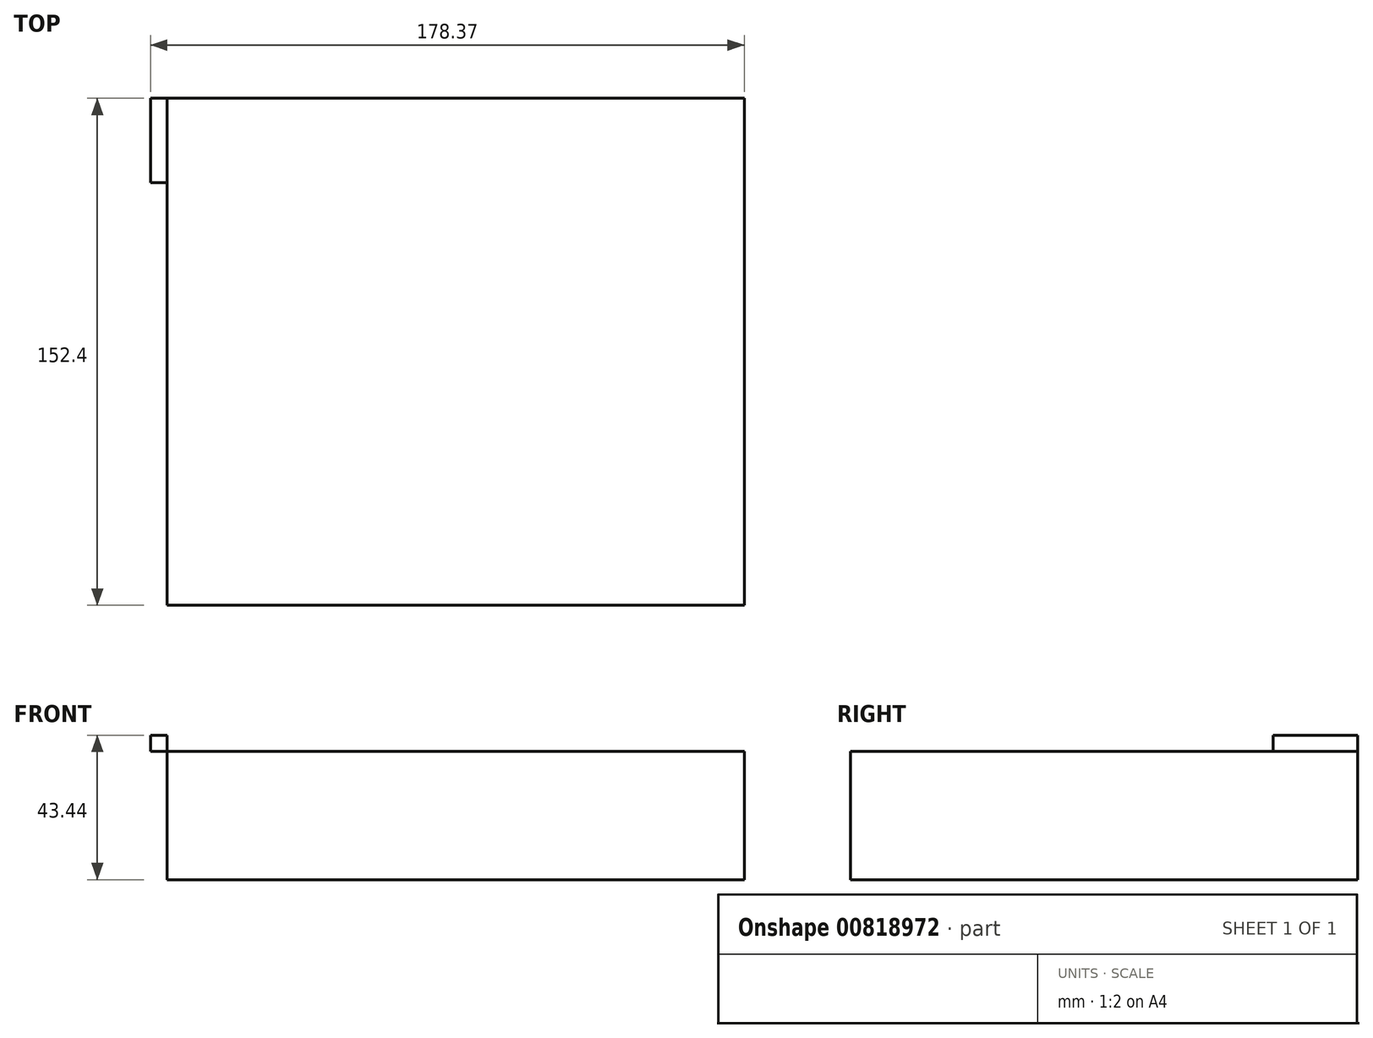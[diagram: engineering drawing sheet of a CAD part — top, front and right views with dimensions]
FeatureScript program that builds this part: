
annotation { "Feature Type Name" : "Feature", "Feature Type Description" : "" }
export const myFeature = defineFeature(function(context is Context, id is Id, definition is map)
    precondition{}
    {
        {
            var Q0;
            Q0=qCreatedBy(makeId("Front.planeOp"),FACE);
            var sketch = newSketch(context, id + "F0", { "sketchPlane" : qUnion([Q0])});
            skLineSegment(sketch, "E0.bottom", {"start": v(-86.74, 19.28) * mm, "end": v(86.74, 19.28) * mm});
            skLineSegment(sketch, "E0.top", {"start": v(-86.74, -19.28) * mm, "end": v(86.74, -19.28) * mm});
            skLineSegment(sketch, "E0.left", {"start": v(-86.74, 19.28) * mm, "end": v(-86.74, -19.28) * mm});
            skLineSegment(sketch, "E0.right", {"start": v(86.74, 19.28) * mm, "end": v(86.74, -19.28) * mm});
            skPoint(sketch, "E0.middle", {"position": v(0, 0) * mm});
            skLineSegment(sketch, "E1.bottom", {"start": v(-86.74, 19.28) * mm, "end": v(-91.63, 19.28) * mm});
            skLineSegment(sketch, "E1.top", {"start": v(-86.74, 24.16) * mm, "end": v(-91.63, 24.16) * mm});
            skLineSegment(sketch, "E1.left", {"start": v(-86.74, 19.28) * mm, "end": v(-86.74, 24.16) * mm});
            skLineSegment(sketch, "E1.right", {"start": v(-91.63, 19.28) * mm, "end": v(-91.63, 24.16) * mm});
            skPoint(sketch, "E1.middle", {"position": v(-89.19, 21.72) * mm});
            skSolve(sketch);
        }
        {
            var Q0;
            Q0=makeQuery(id+"F0.imprint","IMPRINT",FACE,{"disambiguationData":[TD([[makeQuery(id+"F0.imprint","IMPRINT",EDGE,{"derivedFrom":sQuery(id+"F0.wireOp",EDGE,"E1.bottom")}),-1.0]])]});
            var Q1;
            Q1=makeQuery(id+"F0.imprint","IMPRINT",FACE,{"disambiguationData":[TD([[makeQuery(id+"F0.imprint","IMPRINT",EDGE,{"derivedFrom":sQuery(id+"F0.wireOp",EDGE,"E0.bottom")}),-1.0]])]});
            extrude(context, id + "F1", {"entities" : qUnion([Q0, Q1]), "depth" : 25.4 * mm, "offsetDistance" : 25.4 * mm});
        }
        {
            var Q0;
            Q0=makeQuery(id+"F1.opExtrude","CAP_FACE",FACE,{"disambiguationData":[OSD([sQuery(id+"F0.wireOp",EDGE,"E0.bottom"),sQuery(id+"F0.wireOp",EDGE,"E0.top"),sQuery(id+"F0.wireOp",EDGE,"E0.left"),sQuery(id+"F0.wireOp",EDGE,"E0.right")])],"isStart":false});
            extrude(context, id + "F2", {"entities" : qUnion([Q0]), "operationType" : NewBodyOperationType.ADD, "depth" : 127 * mm, "offsetDistance" : 25.4 * mm});
        }
    });
